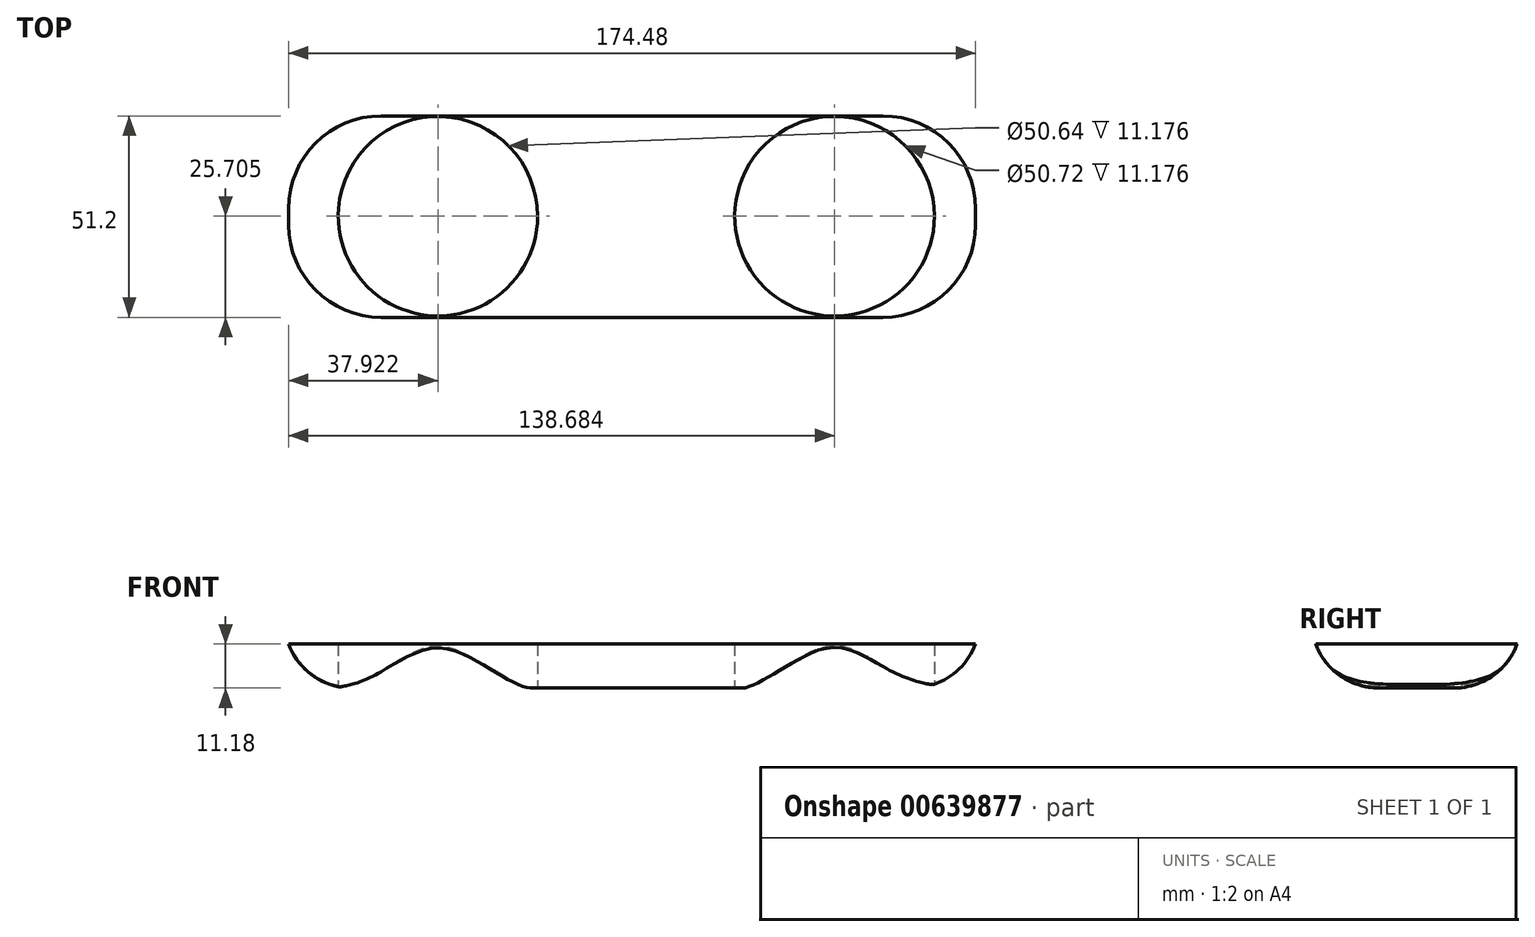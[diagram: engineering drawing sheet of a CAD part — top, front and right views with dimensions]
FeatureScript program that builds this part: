
annotation { "Feature Type Name" : "Feature", "Feature Type Description" : "" }
export const myFeature = defineFeature(function(context is Context, id is Id, definition is map)
    precondition{}
    {
        {
            var Q0;
            Q0=qCreatedBy(makeId("Top.planeOp"),FACE);
            var sketch = newSketch(context, id + "F0", { "sketchPlane" : qUnion([Q0])});
            skPoint(sketch, "E0.middle", {"position": v(0, 11.77) * mm});
            skLineSegment(sketch, "E1.bottom", {"start": v(-57.42, 37.42) * mm, "end": v(70.06, 37.42) * mm});
            skLineSegment(sketch, "E1.top", {"start": v(-57.42, -13.78) * mm, "end": v(70.06, -13.78) * mm});
            skLineSegment(sketch, "E1.left", {"start": v(-80.92, 13.92) * mm, "end": v(-80.92, 9.72) * mm});
            skLineSegment(sketch, "E1.right", {"start": v(93.56, 13.92) * mm, "end": v(93.56, 9.72) * mm});
            skPoint(sketch, "E2.visualSharp", {"position": v(-80.92, 37.42) * mm});
            skArc(sketch, "E2.filletArc", {"start": v(-57.42, 37.42) * mm, "mid": v(-74.04, 30.54) * mm, "end": v(-80.92, 13.92) * mm});
            skPoint(sketch, "E3.visualSharp", {"position": v(-80.92, -13.78) * mm});
            skArc(sketch, "E3.filletArc", {"start": v(-80.92, 9.72) * mm, "mid": v(-74.04, -6.9) * mm, "end": v(-57.42, -13.78) * mm});
            skPoint(sketch, "E4.visualSharp", {"position": v(93.56, 37.42) * mm});
            skArc(sketch, "E4.filletArc", {"start": v(93.56, 13.92) * mm, "mid": v(86.67, 30.54) * mm, "end": v(70.06, 37.42) * mm});
            skPoint(sketch, "E5.visualSharp", {"position": v(93.56, -13.78) * mm});
            skArc(sketch, "E5.filletArc", {"start": v(70.06, -13.78) * mm, "mid": v(86.67, -6.9) * mm, "end": v(93.56, 9.72) * mm});
            skPoint(sketch, "E6.first.point", {"position": v(55.14, -13.78) * mm});
            skPoint(sketch, "E6.second.point", {"position": v(55.72, 37.42) * mm});
            skPoint(sketch, "E6.third.point", {"position": v(36.49, 25) * mm});
            skCircle(sketch, "E7", {"center": v(-43, 11.92) * mm, "radius": 25.32 * mm});
            skCircle(sketch, "E8", {"center": v(57.76, 11.92) * mm, "radius": 25.36 * mm});
            skEllipse(sketch, "E9", {"center": v(-51.63, 21.11) * mm, "majorRadius": 12.16 * mm, "minorRadius": 3.31 * mm, "majorAxis": v(-0.7, 0.7)});
            skSolve(sketch);
        }
        {
            var Q0;
            Q0=makeQuery(id+"F0.imprint","IMPRINT",FACE,{"disambiguationData":[TD([[makeQuery(id+"F0.imprint","IMPRINT",EDGE,{"derivedFrom":sQuery(id+"F0.wireOp",EDGE,"E1.bottom")}),-1.0]])]});
            extrude(context, id + "F1", {"entities" : qUnion([Q0]), "depth" : 11.18 * mm, "offsetDistance" : 25.4 * mm});
        }
        {
            var Q0;
            Q0=makeQuery(id+"F1.opExtrude","CAP_EDGE",EDGE,{"disambiguationData":[OSD([sQuery(id+"F0.wireOp",EDGE,"E3.filletArc")])],"isStart":true});
            fillet(context, id + "F2", {"entities" : qUnion([Q0]), "radius" : 17.17 * mm, "tangentPropagation" : true, "allowEdgeOverflow" : false});
        }
    });
